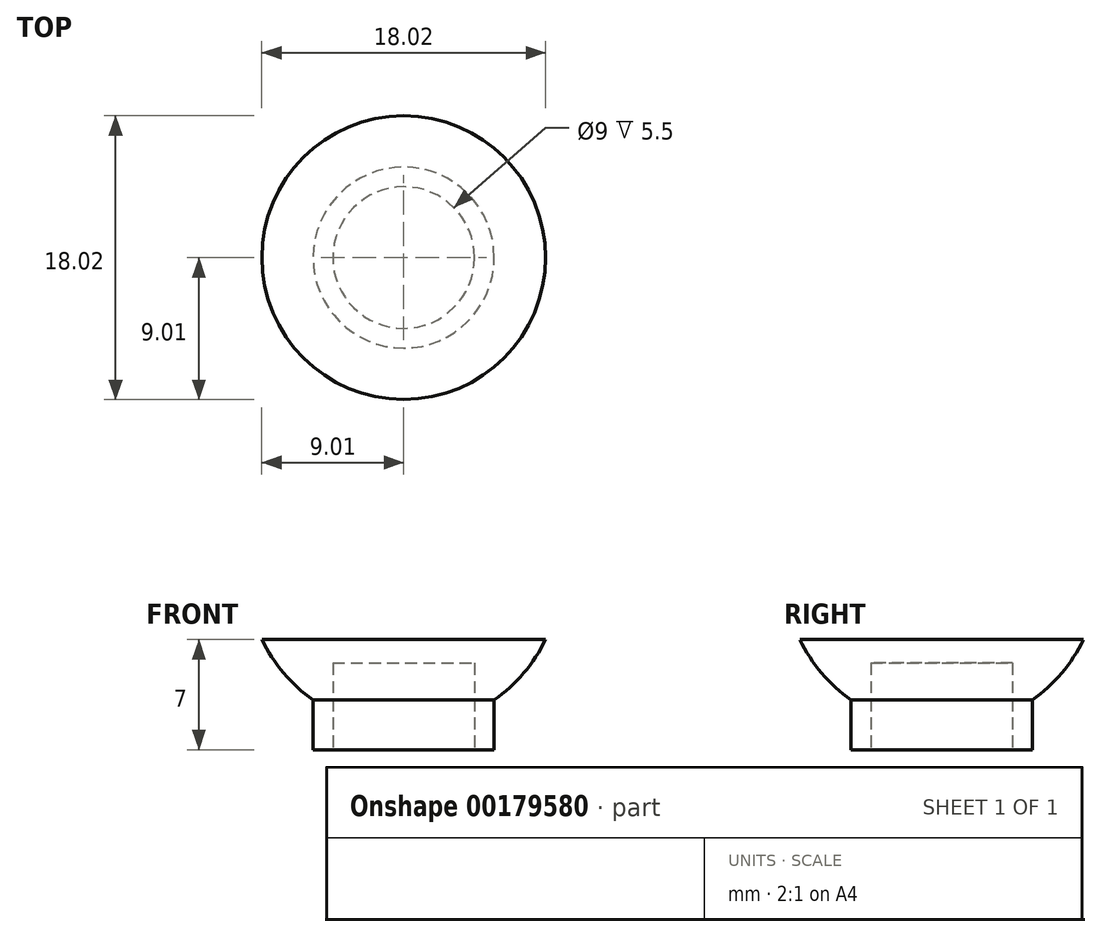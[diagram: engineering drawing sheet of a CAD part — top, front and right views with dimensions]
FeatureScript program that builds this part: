
annotation { "Feature Type Name" : "Feature", "Feature Type Description" : "" }
export const myFeature = defineFeature(function(context is Context, id is Id, definition is map)
    precondition{}
    {
        {
            var Q0;
            Q0=qCreatedBy(makeId("Top.planeOp"),FACE);
            var sketch = newSketch(context, id + "F0", { "sketchPlane" : qUnion([Q0])});
            skCircle(sketch, "E0", {"center": v(0, 0) * mm, "radius": 5.75 * mm});
            skSolve(sketch);
        }
        {
            var Q0;
            Q0=makeQuery(id+"F0.imprint","IMPRINT",FACE,{"disambiguationData":[TD([[makeQuery(id+"F0.imprint","IMPRINT",EDGE,{"derivedFrom":sQuery(id+"F0.wireOp",EDGE,"E0")}),1.0]])]});
            extrude(context, id + "F1", {"entities" : qUnion([Q0]), "depth" : 4 * mm});
        }
        {
            var Q0;
            Q0=makeQuery(id+"F1.opExtrude","CAP_FACE",FACE,{"disambiguationData":[OSD([sQuery(id+"F0.wireOp",EDGE,"E0")])],"isStart":false});
            cPlane(context, id + "F2", {"entities" : qUnion([Q0]), "cplaneType" : CPlaneType.OFFSET, "offset" : 0 * mm, "oppositeDirection" : true, "width" : 152.4 * mm, "height" : 152.4 * mm});
        }
        {
            var Q0;
            Q0=qCreatedBy(makeId("Right.planeOp"),FACE);
            var sketch = newSketch(context, id + "F3", { "sketchPlane" : qUnion([Q0])});
            skCircle(sketch, "E1", {"center": v(0, 10.84) * mm, "radius": 10 * mm});
            skLineSegment(sketch, "E2", {"start": v(0, 10.84) * mm, "end": v(10, 10.84) * mm});
            skLineSegment(sketch, "E3", {"start": v(10, 10.84) * mm, "end": v(-10, 10.84) * mm});
            skSolve(sketch);
        }
        {
            var Q0;
            {var subQ0=sQuery(id+"F3.wireOp",EDGE,"E3");var subQ4=makeQuery(id+"F3.imprint","IMPRINT",VERTEX,{"derivedFrom":subQ0});Q0=makeQuery(id+"F3.imprint","IMPRINT",FACE,{"disambiguationData":[TD([[makeQuery(id+"F3.imprint","IMPRINT",EDGE,{"disambiguationData":[TD([[subQ4,1.0]])],"derivedFrom":subQ0}),-1.0]])]});}
            var Q1;
            Q1=sQuery(id+"F3.wireOp",EDGE,"E3");
            revolve(context, id + "F4", {"operationType" : NewBodyOperationType.ADD, "entities" : qUnion([Q0]), "axis" : qUnion([Q1]), "revolveType" : RevolveType.FULL});
        }
        {
            var Q0;
            Q0=qCreatedBy(id+"F2.planeOp",FACE);
            cPlane(context, id + "F5", {"entities" : qUnion([Q0]), "cplaneType" : CPlaneType.OFFSET, "offset" : 2.5 * mm, "width" : 152.4 * mm, "height" : 152.4 * mm});
        }
        {
            var Q0;
            Q0=qCreatedBy(id+"F5.planeOp",FACE);
            var sketch = newSketch(context, id + "F6", { "sketchPlane" : qUnion([Q0])});
            skCircle(sketch, "E4", {"center": v(0, 0) * mm, "radius": 12.13 * mm});
            skSolve(sketch);
        }
        {
            var Q0;
            Q0=makeQuery(id+"F6.imprint","IMPRINT",FACE,{"disambiguationData":[TD([[makeQuery(id+"F6.imprint","IMPRINT",EDGE,{"derivedFrom":sQuery(id+"F6.wireOp",EDGE,"E4")}),1.0]])]});
            extrude(context, id + "F7", {"entities" : qUnion([Q0]), "operationType" : NewBodyOperationType.REMOVE, "depth" : 25.4 * mm});
        }
        {
            var Q0;
            Q0=makeQuery(id+"F1.opExtrude","CAP_FACE",FACE,{"disambiguationData":[OSD([sQuery(id+"F0.wireOp",EDGE,"E0")])],"isStart":true});
            var sketch = newSketch(context, id + "F8", { "sketchPlane" : qUnion([Q0])});
            skCircle(sketch, "E5", {"center": v(0, 0) * mm, "radius": 4.5 * mm});
            skSolve(sketch);
        }
        {
            var Q0;
            Q0=makeQuery(id+"F8.imprint","IMPRINT",FACE,{"disambiguationData":[TD([[makeQuery(id+"F8.imprint","IMPRINT",EDGE,{"derivedFrom":sQuery(id+"F8.wireOp",EDGE,"E5")}),1.0]])]});
            extrude(context, id + "F9", {"entities" : qUnion([Q0]), "operationType" : NewBodyOperationType.REMOVE, "oppositeDirection" : true, "depth" : 5 * mm});
        }
        {
            var Q0;
            Q0=makeQuery(id+"F1.opExtrude","CAP_FACE",FACE,{"disambiguationData":[OSD([sQuery(id+"F0.wireOp",EDGE,"E0")])],"isStart":true});
            extrude(context, id + "F10", {"entities" : qUnion([Q0]), "operationType" : NewBodyOperationType.ADD, "depth" : 0.5 * mm});
        }
    });
